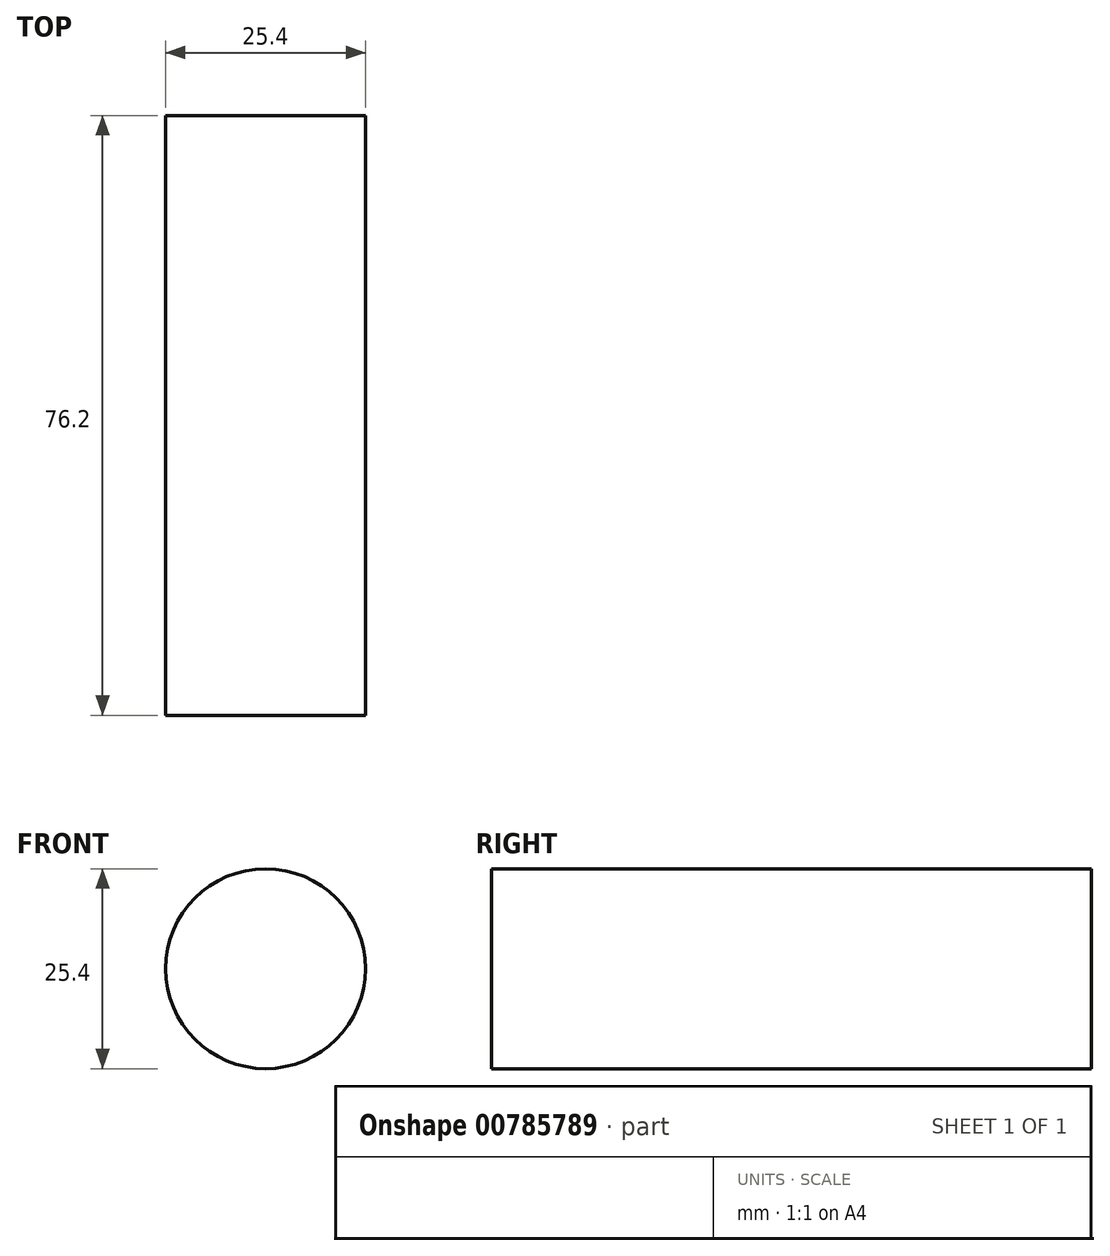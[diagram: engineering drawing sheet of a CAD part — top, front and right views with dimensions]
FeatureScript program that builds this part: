
annotation { "Feature Type Name" : "Feature", "Feature Type Description" : "" }
export const myFeature = defineFeature(function(context is Context, id is Id, definition is map)
    precondition{}
    {
        {
            var Q0;
            Q0=qCreatedBy(makeId("Front.planeOp"),FACE);
            var sketch = newSketch(context, id + "F0", { "sketchPlane" : qUnion([Q0])});
            skCircle(sketch, "E0", {"center": v(-520.87, -147.78) * mm, "radius": 12.7 * mm});
            skSolve(sketch);
        }
        {
            var Q0;
            Q0=makeQuery(id+"F0.imprint","IMPRINT",FACE,{"disambiguationData":[TD([[makeQuery(id+"F0.imprint","IMPRINT",EDGE,{"derivedFrom":sQuery(id+"F0.wireOp",EDGE,"E0")}),1.0]])]});
            extrude(context, id + "F1", {"entities" : qUnion([Q0]), "depth" : 76.2 * mm, "offsetDistance" : 25.4 * mm});
        }
    });
